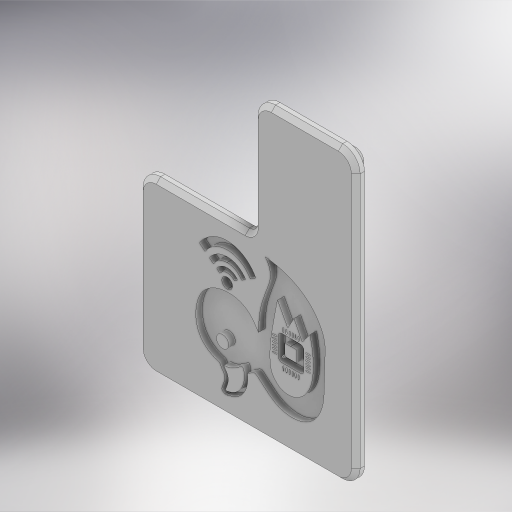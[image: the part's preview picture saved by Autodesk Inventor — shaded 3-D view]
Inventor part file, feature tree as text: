
AUTODESK INVENTOR PART (.ipt)
format: ipt  version: 2024 (Build 280153000, 153)  size: 755,200 bytes
history: native  units: mm
features: extrude x3, sketch x3, other x3, reference x2, chamfer x1
ambient origin geometry x8: Origin, YZ Plane, XZ Plane, XY Plane, X Axis, Y Axis, Z Axis, Center Point
bodies: Solid1 (feature_tree)
feature tree (12):
  extrude  "Extrusion1"  Depth=2.0mm TaperAngle=0.0deg
  extrude  "Extrusion2"  Depth=0.2mm
  chamfer  "Chamfer1"  Distance=1.5mm
  extrude  "Extrusion3"  [1 undecoded]
  sketch  "Sketch1"  dims[d1=2.0mm d2=0.0mm d3=2.0mm d4=0.0mm]
  reference  "Reference1"
  sketch  "Sketch2"  dims[d5=1.0mm d6=2.0mm d7=45.0deg d8=0.2mm d9=1.5mm d10=0.0mm]
  reference  "Reference2"
  sketch  "Sketch4"
  other  "<userpath>\Documents\Uni 2024 T3\COMP6841\CAD\Whole thing.iam"
  other  "Whole thing.iam"
  other  "Case:1"
note: 1 required parameter value undecoded (feature->parameter linkage not recoverable at this tier; creation-order binding heuristic only, values carry confidence <= 0.55)
